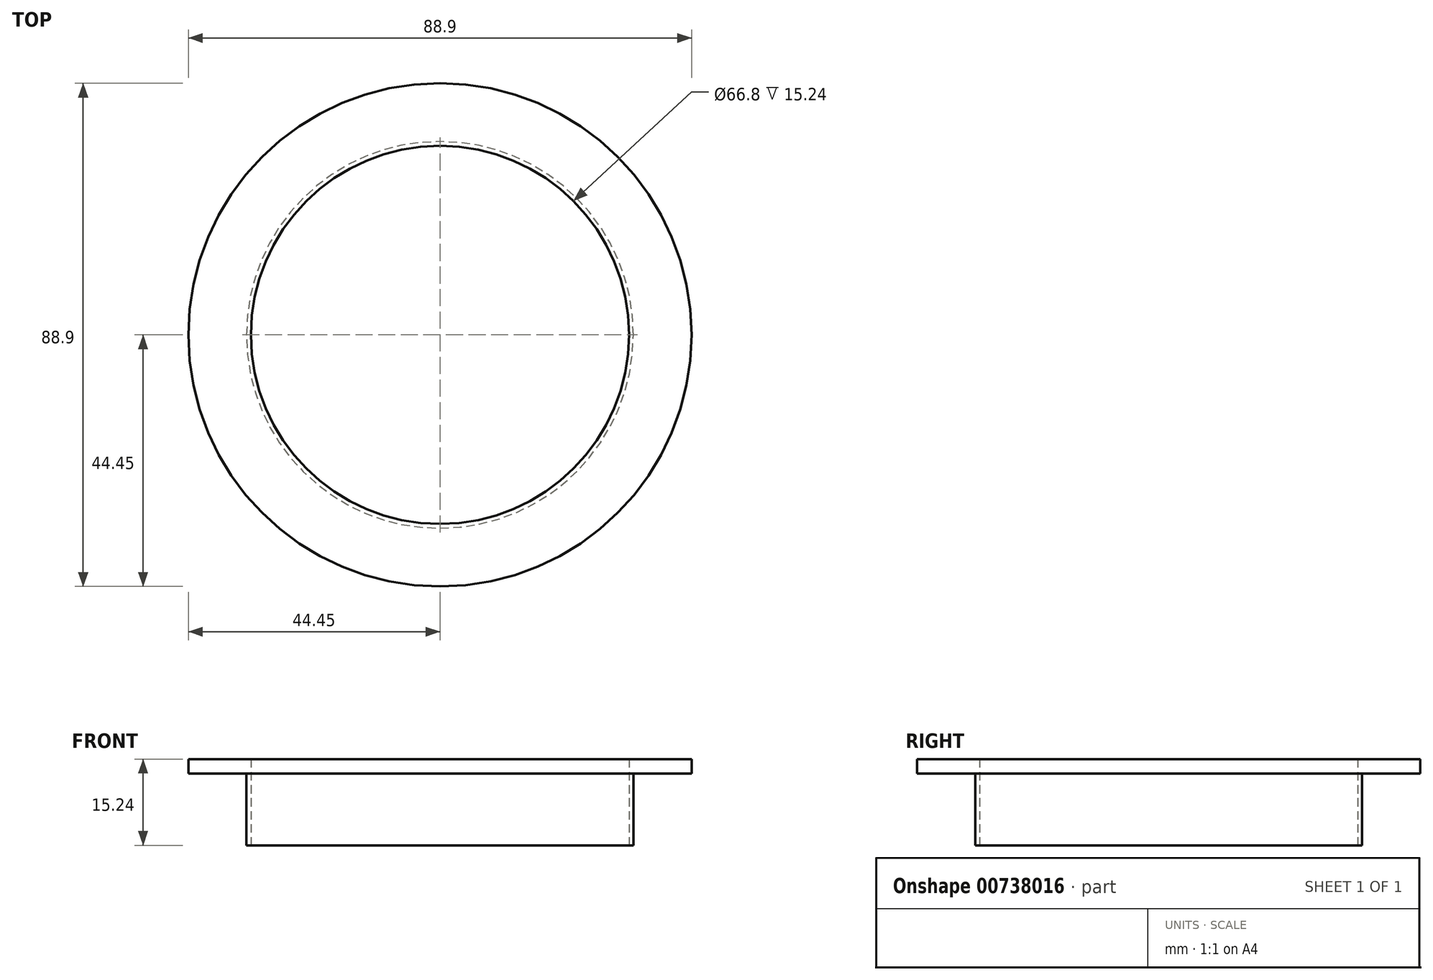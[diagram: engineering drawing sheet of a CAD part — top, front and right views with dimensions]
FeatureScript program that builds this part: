
annotation { "Feature Type Name" : "Feature", "Feature Type Description" : "" }
export const myFeature = defineFeature(function(context is Context, id is Id, definition is map)
    precondition{}
    {
        {
            var Q0;
            Q0=qCreatedBy(makeId("Top.planeOp"),FACE);
            var sketch = newSketch(context, id + "F0", { "sketchPlane" : qUnion([Q0])});
            skCircle(sketch, "E0", {"center": v(0, 0) * mm, "radius": 44.45 * mm});
            skCircle(sketch, "E1", {"center": v(0, 0) * mm, "radius": 34.16 * mm});
            skCircle(sketch, "E2", {"center": v(0, 0) * mm, "radius": 33.4 * mm});
            skSolve(sketch);
        }
        {
            var Q0;
            Q0=qSketchRegion(id+"F0",true);
            extrude(context, id + "F1", {"entities" : qUnion([Q0]), "depth" : 2.54 * mm, "offsetDistance" : 25.4 * mm});
        }
        {
            var Q0;
            Q0=makeQuery(id+"F0.imprint","IMPRINT",FACE,{"disambiguationData":[TD([[makeQuery(id+"F0.imprint","IMPRINT",EDGE,{"derivedFrom":sQuery(id+"F0.wireOp",EDGE,"E1")}),1.0]])]});
            extrude(context, id + "F2", {"entities" : qUnion([Q0]), "operationType" : NewBodyOperationType.ADD, "depth" : 2.54 * mm, "offsetDistance" : 25.4 * mm, "hasSecondDirection" : true, "secondDirectionOppositeDirection" : true, "secondDirectionDepth" : 12.7 * mm});
        }
    });
